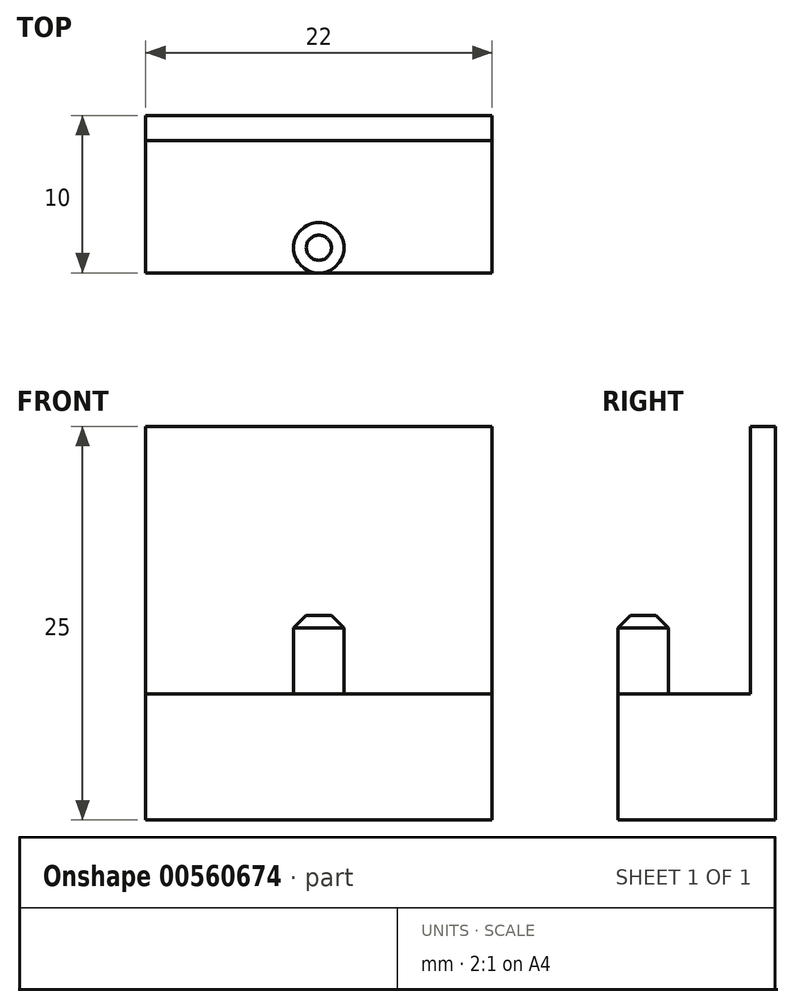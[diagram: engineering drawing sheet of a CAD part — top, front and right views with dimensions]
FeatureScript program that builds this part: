
annotation { "Feature Type Name" : "Feature", "Feature Type Description" : "" }
export const myFeature = defineFeature(function(context is Context, id is Id, definition is map)
    precondition{}
    {
        {
            var Q0;
            Q0=qCreatedBy(makeId("Top.planeOp"),FACE);
            var sketch = newSketch(context, id + "F0", { "sketchPlane" : qUnion([Q0])});
            skLineSegment(sketch, "E0.bottom", {"start": v(-4.66, 3.46) * mm, "end": v(-26.66, 3.46) * mm});
            skLineSegment(sketch, "E0.top", {"start": v(-4.66, 13.46) * mm, "end": v(-26.66, 13.46) * mm});
            skLineSegment(sketch, "E0.left", {"start": v(-4.66, 3.46) * mm, "end": v(-4.66, 13.46) * mm});
            skLineSegment(sketch, "E0.right", {"start": v(-26.66, 3.46) * mm, "end": v(-26.66, 13.46) * mm});
            skPoint(sketch, "E0.middle", {"position": v(-15.66, 8.46) * mm});
            skLineSegment(sketch, "E1", {"start": v(-26.66, 11.86) * mm, "end": v(-4.66, 11.86) * mm});
            skCircle(sketch, "E2", {"center": v(-15.66, 5.06) * mm, "radius": 1.6 * mm});
            skSolve(sketch);
        }
        {
            var Q0;
            {var subQ3=sQuery(id+"F0.wireOp",EDGE,"E1");Q0=makeQuery(id+"F0.imprint","IMPRINT",FACE,{"disambiguationData":[TD([[makeQuery(id+"F0.imprint","IMPRINT",EDGE,{"derivedFrom":subQ3}),-1.0]])]});}
            var Q1;
            {var subQ0=sQuery(id+"F0.wireOp",EDGE,"E0.top");Q1=makeQuery(id+"F0.imprint","IMPRINT",FACE,{"disambiguationData":[TD([[makeQuery(id+"F0.imprint","IMPRINT",EDGE,{"derivedFrom":subQ0}),1.0]])]});}
            var Q2;
            Q2=makeQuery(id+"F0.imprint","IMPRINT",FACE,{"disambiguationData":[TD([[makeQuery(id+"F0.imprint","IMPRINT",EDGE,{"derivedFrom":sQuery(id+"F0.wireOp",EDGE,"E2")}),1.0]])]});
            extrude(context, id + "F1", {"entities" : qUnion([Q0, Q1, Q2]), "depth" : 8 * mm, "offsetDistance" : 25 * mm});
        }
        {
            var Q0;
            {var subQ0=sQuery(id+"F0.wireOp",EDGE,"E0.top");Q0=makeQuery(id+"F0.imprint","IMPRINT",FACE,{"disambiguationData":[TD([[makeQuery(id+"F0.imprint","IMPRINT",EDGE,{"derivedFrom":subQ0}),1.0]])]});}
            extrude(context, id + "F2", {"entities" : qUnion([Q0]), "operationType" : NewBodyOperationType.ADD, "depth" : 25 * mm, "offsetDistance" : 25 * mm});
        }
        {
            var Q0;
            Q0=makeQuery(id+"F0.imprint","IMPRINT",FACE,{"disambiguationData":[TD([[makeQuery(id+"F0.imprint","IMPRINT",EDGE,{"derivedFrom":sQuery(id+"F0.wireOp",EDGE,"E2")}),1.0]])]});
            extrude(context, id + "F3", {"entities" : qUnion([Q0]), "operationType" : NewBodyOperationType.ADD, "depth" : 13 * mm, "offsetDistance" : 25 * mm});
        }
        {
            var Q0;
            Q0=makeQuery(id+"F3.opExtrude","CAP_EDGE",EDGE,{"disambiguationData":[OSD([sQuery(id+"F0.wireOp",EDGE,"E2")])],"isStart":false});
            chamfer(context, id + "F4", {"entities" : qUnion([Q0]), "width" : 0.8 * mm, "tangentPropagation" : true});
        }
    });
